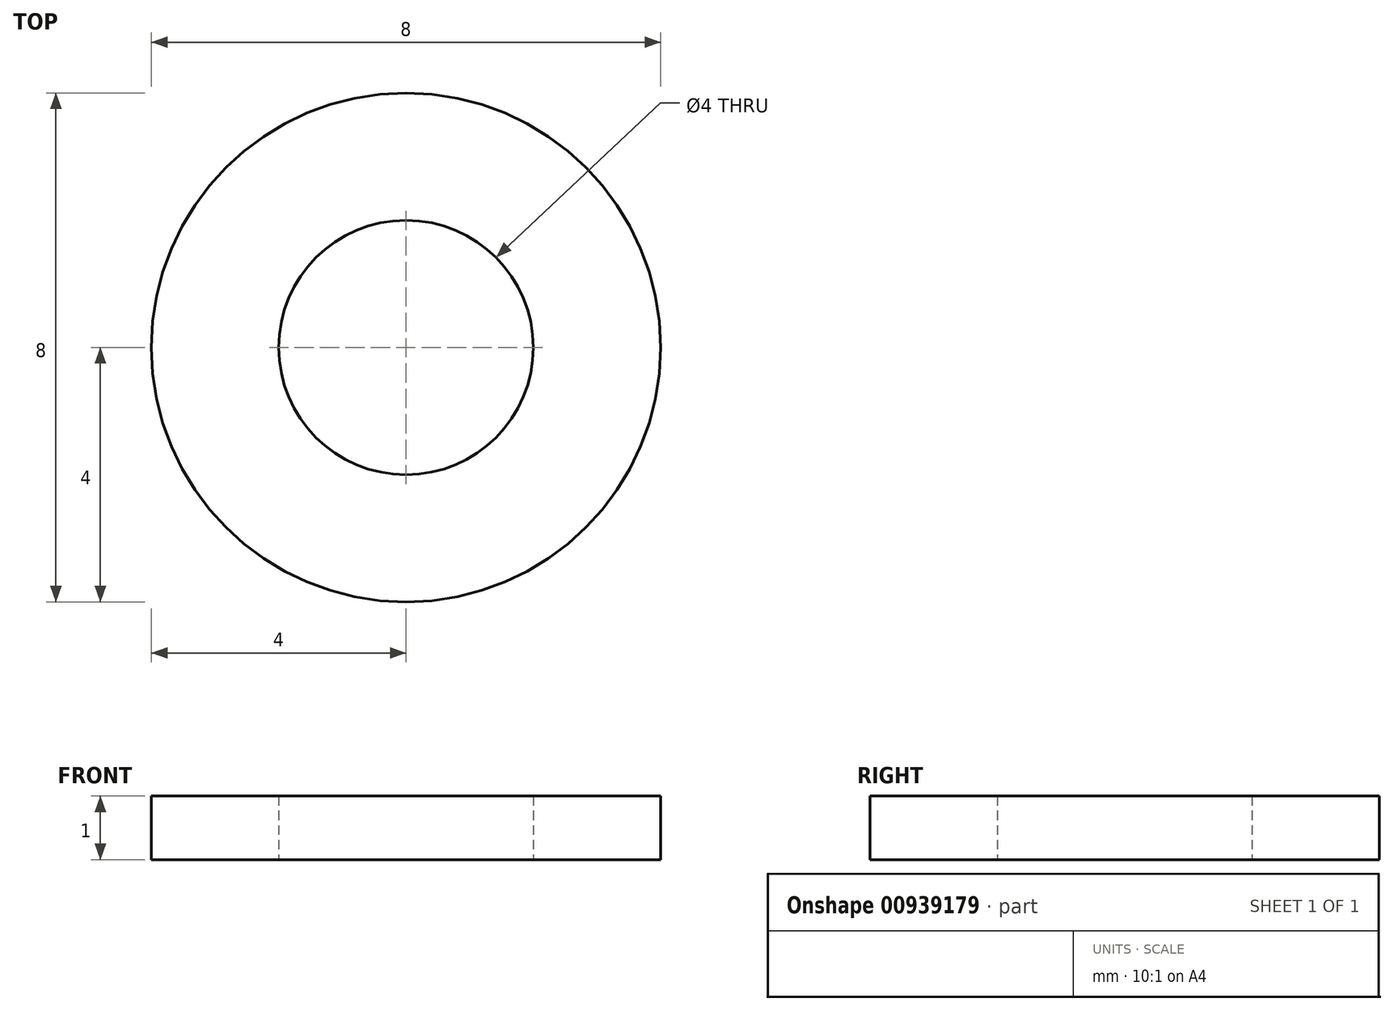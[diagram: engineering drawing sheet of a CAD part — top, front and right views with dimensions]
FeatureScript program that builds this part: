
annotation { "Feature Type Name" : "Feature", "Feature Type Description" : "" }
export const myFeature = defineFeature(function(context is Context, id is Id, definition is map)
    precondition{}
    {
        {
            var Q0;
            Q0=qCreatedBy(makeId("Top.planeOp"),FACE);
            var sketch = newSketch(context, id + "F0", { "sketchPlane" : qUnion([Q0])});
            skCircle(sketch, "E0", {"center": v(0, 0) * mm, "radius": 2 * mm});
            skCircle(sketch, "E1", {"center": v(0, 0) * mm, "radius": 4 * mm});
            skSolve(sketch);
        }
        {
            var Q0;
            Q0=makeQuery(id+"F0.imprint","IMPRINT",FACE,{"disambiguationData":[TD([[makeQuery(id+"F0.imprint","IMPRINT",EDGE,{"derivedFrom":sQuery(id+"F0.wireOp",EDGE,"E0")}),-1.0]])]});
            extrude(context, id + "F1", {"entities" : qUnion([Q0]), "depth" : 1 * mm, "offsetDistance" : 25 * mm});
        }
    });
